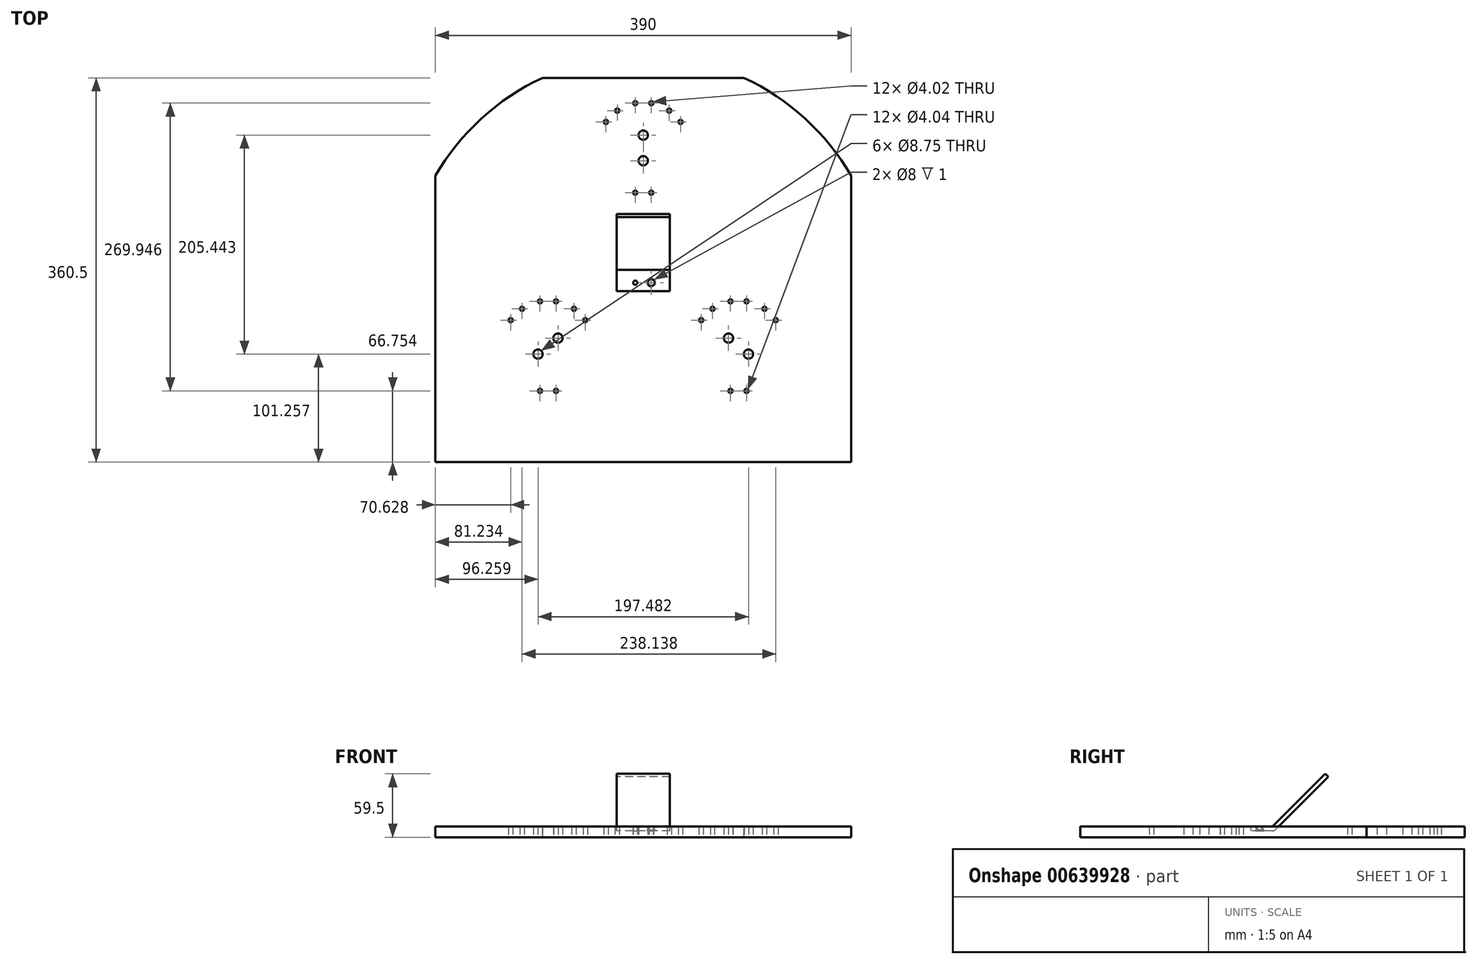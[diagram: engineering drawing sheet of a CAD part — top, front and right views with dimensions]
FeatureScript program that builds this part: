
annotation { "Feature Type Name" : "Feature", "Feature Type Description" : "" }
export const myFeature = defineFeature(function(context is Context, id is Id, definition is map)
    precondition{}
    {
        {
            var Q0;
            Q0=qCreatedBy(makeId("Top.planeOp"),FACE);
            var sketch = newSketch(context, id + "F0", { "sketchPlane" : qUnion([Q0])});
            skLineSegment(sketch, "E0.bottom", {"start": v(195, -180.25) * mm, "end": v(-195, -180.25) * mm});
            skLineSegment(sketch, "E0.left", {"start": v(195, -180.25) * mm, "end": v(195, 88.25) * mm});
            skLineSegment(sketch, "E0.right", {"start": v(-195, -180.25) * mm, "end": v(-195, 88.25) * mm});
            skLineSegment(sketch, "E1", {"start": v(-94.38, 180.25) * mm, "end": v(94.38, 180.25) * mm});
            skArc(sketch, "E2", {"start": v(-94.38, 180.25) * mm, "mid": v(-151.82, 142.06) * mm, "end": v(-195, 88.25) * mm});
            skArc(sketch, "E3", {"start": v(195, 88.25) * mm, "mid": v(151.82, 142.06) * mm, "end": v(94.38, 180.25) * mm});
            skCircle(sketch, "E4", {"center": v(0, 0) * mm, "radius": 126.45 * mm, "construction": true});
            skCircle(sketch, "E5", {"center": v(0, 0) * mm, "radius": 102.45 * mm, "construction": true});
            skLineSegment(sketch, "E6", {"start": v(-98.74, -79) * mm, "end": v(0, 0) * mm, "construction": true});
            skLineSegment(sketch, "E7", {"start": v(98.74, -79) * mm, "end": v(0, 0) * mm, "construction": true});
            skPoint(sketch, "E8", {"position": v(0, 126.45) * mm});
            skPoint(sketch, "E9", {"position": v(0, 102.45) * mm});
            skPoint(sketch, "E10", {"position": v(80, -64) * mm});
            skPoint(sketch, "E11", {"position": v(98.74, -79) * mm});
            skPoint(sketch, "E12", {"position": v(-80, -64) * mm});
            skPoint(sketch, "E13", {"position": v(-98.74, -79) * mm});
            skSolve(sketch);
        }
        {
            var Q0;
            Q0 = qSketchRegion(id + "F0", true);
            extrude(context, id + "F1", {"entities" : qUnion([Q0]), "oppositeDirection" : true, "depth" : 10 * mm, "offsetDistance" : 25 * mm});
        }
        {
            var Q0;
            Q0=sQuery(id+"F0.wireOp",VERTEX,"E8");
            var Q1;
            Q1=sQuery(id+"F0.wireOp",VERTEX,"E9");
            var Q2;
            Q2=sQuery(id+"F0.wireOp",VERTEX,"E12");
            var Q3;
            Q3=sQuery(id+"F0.wireOp",VERTEX,"E13");
            var Q4;
            Q4=sQuery(id+"F0.wireOp",VERTEX,"E10");
            var Q5;
            Q5=sQuery(id+"F0.wireOp",VERTEX,"E11");
            var Q6;
            Q6=makeQuery(id+"F1.opExtrude","SWEPT_BODY",BODY,{"disambiguationData":[OSD([sQuery(id+"F0.wireOp",EDGE,"E0.bottom"),sQuery(id+"F0.wireOp",EDGE,"E0.left"),sQuery(id+"F0.wireOp",EDGE,"E0.right"),sQuery(id+"F0.wireOp",EDGE,"E1"),sQuery(id+"F0.wireOp",EDGE,"E2"),sQuery(id+"F0.wireOp",EDGE,"E3")])]});
            hole(context, id + "F2", {"style" : HoleStyle.SIMPLE, "endStyle" : HoleEndStyle.THROUGH, "holeDiameter" : 8.75 * mm, "majorDiameter" : 5 * mm, "isTappedThrough" : true, "tappedDepth" : 12 * mm, "tapClearance" : 3, "locations" : qUnion([Q0, Q1, Q2, Q3, Q4, Q5]), "scope" : qUnion([Q6]), "startStyle" : HoleStartStyle.PART});
        }
        {
            var Q0;
            Q0=makeQuery(id+"F1.opExtrude","CAP_FACE",FACE,{"disambiguationData":[OSD([sQuery(id+"F0.wireOp",EDGE,"E0.bottom"),sQuery(id+"F0.wireOp",EDGE,"E0.left"),sQuery(id+"F0.wireOp",EDGE,"E0.right"),sQuery(id+"F0.wireOp",EDGE,"xNgbPUBY-uuYC-CHOZ-C7bY-90BZvyAFI4Vc"),sQuery(id+"F0.wireOp",EDGE,"pYRuWuoG-lrcK-cojv-Qarx-NnTwJ9ShBMCn"),sQuery(id+"F0.wireOp",EDGE,"e0wAC1A8-toIX-Gtfu-GmEW-TRQK8LJyyQk8"),sQuery(id+"F0.wireOp",EDGE,"2FMPs9kU-bOJq-Ht3o-1aew-Xf9CLyV6Ygsu"),sQuery(id+"F0.wireOp",EDGE,"OQ8i2MKw-3ids-VtER-UMBf-tPz4OA3PYS6q"),sQuery(id+"F0.wireOp",EDGE,"hYeVSYyp-zt9g-Qamr-OxOk-HJPD7gPKY8dS"),sQuery(id+"F0.wireOp",EDGE,"E1"),sQuery(id+"F0.wireOp",EDGE,"E2"),sQuery(id+"F0.wireOp",EDGE,"E3")])],"isStart":true});
            var sketch = newSketch(context, id + "F3", { "sketchPlane" : qUnion([Q0])});
            skLineSegment(sketch, "E14", {"start": v(0, 126.45) * mm, "end": v(0, 102.45) * mm, "construction": true});
            skPoint(sketch, "E15.1.0", {"position": v(7.5, 72.45) * mm});
            skLineSegment(sketch, "E15.1.1", {"start": v(7.5, 72.45) * mm, "end": v(-7.5, 72.45) * mm, "construction": true});
            skPoint(sketch, "E15.1.3", {"position": v(-7.5, 72.45) * mm});
            skPoint(sketch, "E16", {"position": v(0, 114.45) * mm});
            skPoint(sketch, "E17", {"position": v(0, 72.45) * mm});
            skPoint(sketch, "E18.1.0", {"position": v(-35, 138.85) * mm});
            skLineSegment(sketch, "E18.1.1", {"start": v(-35, 138.85) * mm, "end": v(-24.4, 149.45) * mm, "construction": true});
            skPoint(sketch, "E18.1.2", {"position": v(-24.4, 149.45) * mm});
            skPoint(sketch, "E18.1.3", {"position": v(-29.7, 144.15) * mm});
            skLineSegment(sketch, "E18.anchor1", {"start": v(0, 114.45) * mm, "end": v(0, 72.45) * mm, "construction": true});
            skLineSegment(sketch, "E18.anchor2", {"start": v(0, 114.45) * mm, "end": v(-29.7, 144.15) * mm, "construction": true});
            skPoint(sketch, "E19.1.0", {"position": v(7.5, 156.45) * mm});
            skLineSegment(sketch, "E19.1.1", {"start": v(-7.5, 156.45) * mm, "end": v(7.5, 156.45) * mm, "construction": true});
            skPoint(sketch, "E19.1.2", {"position": v(0, 156.45) * mm});
            skPoint(sketch, "E19.1.3", {"position": v(-7.5, 156.45) * mm});
            skPoint(sketch, "E19.2.0", {"position": v(35, 138.85) * mm});
            skLineSegment(sketch, "E19.2.1", {"start": v(24.4, 149.45) * mm, "end": v(35, 138.85) * mm, "construction": true});
            skPoint(sketch, "E19.2.2", {"position": v(29.7, 144.15) * mm});
            skPoint(sketch, "E19.2.3", {"position": v(24.4, 149.45) * mm});
            skLineSegment(sketch, "E19.anchor2", {"start": v(0, 114.45) * mm, "end": v(29.7, 144.15) * mm, "construction": true});
            skPoint(sketch, "E20.1.0", {"position": v(96.87, -113.5) * mm});
            skLineSegment(sketch, "E20.1.1", {"start": v(96.87, -113.5) * mm, "end": v(81.87, -113.5) * mm, "construction": true});
            skPoint(sketch, "E20.1.3", {"position": v(81.87, -113.5) * mm});
            skPoint(sketch, "E21", {"position": v(89.37, -71.5) * mm});
            skPoint(sketch, "E22", {"position": v(89.37, -113.5) * mm});
            skPoint(sketch, "E23.1.0", {"position": v(54.37, -47.1) * mm});
            skLineSegment(sketch, "E23.1.1", {"start": v(54.37, -47.1) * mm, "end": v(64.98, -36.5) * mm, "construction": true});
            skPoint(sketch, "E23.1.2", {"position": v(64.98, -36.5) * mm});
            skPoint(sketch, "E23.1.3", {"position": v(59.67, -41.8) * mm});
            skLineSegment(sketch, "E23.anchor1", {"start": v(89.37, -71.5) * mm, "end": v(89.37, -113.5) * mm, "construction": true});
            skLineSegment(sketch, "E23.anchor2", {"start": v(89.37, -71.5) * mm, "end": v(59.67, -41.8) * mm, "construction": true});
            skPoint(sketch, "E24.1.0", {"position": v(96.87, -29.5) * mm});
            skLineSegment(sketch, "E24.1.1", {"start": v(81.87, -29.5) * mm, "end": v(96.87, -29.5) * mm, "construction": true});
            skPoint(sketch, "E24.1.2", {"position": v(89.37, -29.5) * mm});
            skPoint(sketch, "E24.1.3", {"position": v(81.87, -29.5) * mm});
            skPoint(sketch, "E24.2.0", {"position": v(124.37, -47.1) * mm});
            skLineSegment(sketch, "E24.2.1", {"start": v(113.77, -36.5) * mm, "end": v(124.37, -47.1) * mm, "construction": true});
            skPoint(sketch, "E24.2.2", {"position": v(119.07, -41.8) * mm});
            skPoint(sketch, "E24.2.3", {"position": v(113.77, -36.5) * mm});
            skLineSegment(sketch, "E24.anchor2", {"start": v(89.37, -71.5) * mm, "end": v(119.07, -41.8) * mm, "construction": true});
            skLineSegment(sketch, "E25", {"start": v(80, -64) * mm, "end": v(98.74, -79) * mm, "construction": true});
            skPoint(sketch, "E26.1.0", {"position": v(-81.87, -113.5) * mm});
            skLineSegment(sketch, "E26.1.1", {"start": v(-81.87, -113.5) * mm, "end": v(-96.87, -113.5) * mm, "construction": true});
            skPoint(sketch, "E26.1.3", {"position": v(-96.87, -113.5) * mm});
            skPoint(sketch, "E27", {"position": v(-89.37, -71.5) * mm});
            skPoint(sketch, "E28", {"position": v(-89.37, -113.5) * mm});
            skPoint(sketch, "E29.1.0", {"position": v(-124.37, -47.1) * mm});
            skLineSegment(sketch, "E29.1.1", {"start": v(-124.37, -47.1) * mm, "end": v(-113.77, -36.5) * mm, "construction": true});
            skPoint(sketch, "E29.1.2", {"position": v(-113.77, -36.5) * mm});
            skPoint(sketch, "E29.1.3", {"position": v(-119.07, -41.8) * mm});
            skLineSegment(sketch, "E29.anchor1", {"start": v(-89.37, -71.5) * mm, "end": v(-89.37, -113.5) * mm, "construction": true});
            skLineSegment(sketch, "E29.anchor2", {"start": v(-89.37, -71.5) * mm, "end": v(-119.07, -41.8) * mm, "construction": true});
            skPoint(sketch, "E30.1.0", {"position": v(-81.87, -29.5) * mm});
            skLineSegment(sketch, "E30.1.1", {"start": v(-96.87, -29.5) * mm, "end": v(-81.87, -29.5) * mm, "construction": true});
            skPoint(sketch, "E30.1.2", {"position": v(-89.37, -29.5) * mm});
            skPoint(sketch, "E30.1.3", {"position": v(-96.87, -29.5) * mm});
            skPoint(sketch, "E30.2.0", {"position": v(-54.37, -47.1) * mm});
            skLineSegment(sketch, "E30.2.1", {"start": v(-64.98, -36.5) * mm, "end": v(-54.37, -47.1) * mm, "construction": true});
            skPoint(sketch, "E30.2.2", {"position": v(-59.67, -41.8) * mm});
            skPoint(sketch, "E30.2.3", {"position": v(-64.98, -36.5) * mm});
            skLineSegment(sketch, "E30.anchor2", {"start": v(-89.37, -71.5) * mm, "end": v(-59.67, -41.8) * mm, "construction": true});
            skLineSegment(sketch, "E31", {"start": v(-80, -64) * mm, "end": v(-98.74, -79) * mm, "construction": true});
            skSolve(sketch);
        }
        {
            var Q0;
            Q0=sQuery(id+"F3.wireOp",VERTEX,"E15.1.3");
            var Q1;
            Q1=sQuery(id+"F3.wireOp",VERTEX,"E20.1.3");
            var Q2;
            Q2=sQuery(id+"F3.wireOp",VERTEX,"E26.1.3");
            var Q3;
            Q3=sQuery(id+"F3.wireOp",VERTEX,"E29.1.2");
            var Q4;
            Q4=sQuery(id+"F3.wireOp",VERTEX,"E30.1.0");
            var Q5;
            Q5=sQuery(id+"F3.wireOp",VERTEX,"E30.2.0");
            var Q6;
            Q6=sQuery(id+"F3.wireOp",VERTEX,"E23.1.2");
            var Q7;
            Q7=sQuery(id+"F3.wireOp",VERTEX,"E24.1.0");
            var Q8;
            Q8=sQuery(id+"F3.wireOp",VERTEX,"E24.2.0");
            var Q9;
            Q9=sQuery(id+"F3.wireOp",VERTEX,"E18.1.2");
            var Q10;
            Q10=sQuery(id+"F3.wireOp",VERTEX,"E19.1.0");
            var Q11;
            Q11=sQuery(id+"F3.wireOp",VERTEX,"E19.2.0");
            var Q12;
            Q12=makeQuery(id+"F1.opExtrude","SWEPT_BODY",BODY,{"disambiguationData":[OSD([sQuery(id+"F0.wireOp",EDGE,"E0.bottom"),sQuery(id+"F0.wireOp",EDGE,"E0.left"),sQuery(id+"F0.wireOp",EDGE,"E0.right"),sQuery(id+"F0.wireOp",EDGE,"E1"),sQuery(id+"F0.wireOp",EDGE,"E2"),sQuery(id+"F0.wireOp",EDGE,"E3")])]});
            hole(context, id + "F4", {"style" : HoleStyle.SIMPLE, "endStyle" : HoleEndStyle.THROUGH, "holeDiameter" : 4 * mm, "majorDiameter" : 5 * mm, "isTappedThrough" : true, "tappedDepth" : 12 * mm, "tapClearance" : 3, "locations" : qUnion([Q0, Q1, Q2, Q3, Q4, Q5, Q6, Q7, Q8, Q9, Q10, Q11]), "scope" : qUnion([Q12]), "startStyle" : HoleStartStyle.PART});
        }
        {
            var Q0;
            Q0=sQuery(id+"F3.wireOp",VERTEX,"E15.1.0");
            var Q1;
            Q1=sQuery(id+"F3.wireOp",VERTEX,"E19.2.3");
            var Q2;
            Q2=sQuery(id+"F3.wireOp",VERTEX,"E19.1.3");
            var Q3;
            Q3=sQuery(id+"F3.wireOp",VERTEX,"E18.1.0");
            var Q4;
            Q4=sQuery(id+"F3.wireOp",VERTEX,"E26.1.0");
            var Q5;
            Q5=sQuery(id+"F3.wireOp",VERTEX,"E30.2.3");
            var Q6;
            Q6=sQuery(id+"F3.wireOp",VERTEX,"E30.1.3");
            var Q7;
            Q7=sQuery(id+"F3.wireOp",VERTEX,"E29.1.0");
            var Q8;
            Q8=sQuery(id+"F3.wireOp",VERTEX,"E20.1.0");
            var Q9;
            Q9=sQuery(id+"F3.wireOp",VERTEX,"E24.2.3");
            var Q10;
            Q10=sQuery(id+"F3.wireOp",VERTEX,"E24.1.3");
            var Q11;
            Q11=sQuery(id+"F3.wireOp",VERTEX,"E23.1.0");
            var Q12;
            Q12=makeQuery(id+"F1.opExtrude","SWEPT_BODY",BODY,{"disambiguationData":[OSD([sQuery(id+"F0.wireOp",EDGE,"E0.bottom"),sQuery(id+"F0.wireOp",EDGE,"E0.left"),sQuery(id+"F0.wireOp",EDGE,"E0.right"),sQuery(id+"F0.wireOp",EDGE,"E1"),sQuery(id+"F0.wireOp",EDGE,"E2"),sQuery(id+"F0.wireOp",EDGE,"E3")])]});
            hole(context, id + "F5", {"style" : HoleStyle.SIMPLE, "endStyle" : HoleEndStyle.THROUGH, "holeDiameter" : 4.04 * mm, "majorDiameter" : 5 * mm, "isTappedThrough" : true, "tappedDepth" : 12 * mm, "tapClearance" : 3, "locations" : qUnion([Q0, Q1, Q2, Q3, Q4, Q5, Q6, Q7, Q8, Q9, Q10, Q11]), "scope" : qUnion([Q12]), "startStyle" : HoleStartStyle.PART});
        }
        {
            var Q0;
            Q0=qCreatedBy(makeId("Right.planeOp"),FACE);
            var sketch = newSketch(context, id + "F6", { "sketchPlane" : qUnion([Q0])});
            skLineSegment(sketch, "E32", {"start": v(0, 0) * mm, "end": v(49.5, 49.5) * mm});
            skLineSegment(sketch, "E33", {"start": v(49.5, 49.5) * mm, "end": v(52.33, 46.67) * mm});
            skLineSegment(sketch, "E34", {"start": v(52.33, 46.67) * mm, "end": v(2.83, -2.83) * mm});
            skLineSegment(sketch, "E35", {"start": v(0, -4) * mm, "end": v(-20, -4) * mm});
            skLineSegment(sketch, "E36", {"start": v(-20, -4) * mm, "end": v(-20, 0) * mm});
            skLineSegment(sketch, "E37", {"start": v(-20, 0) * mm, "end": v(0, 0) * mm});
            skPoint(sketch, "E38.visualSharp", {"position": v(1.66, -4) * mm});
            skArc(sketch, "E38.filletArc", {"start": v(0, -4) * mm, "mid": v(1.53, -3.7) * mm, "end": v(2.83, -2.83) * mm});
            skSolve(sketch);
        }
        {
            var Q0;
            Q0 = qSketchRegion(id + "F6", true);
            extrude(context, id + "F7", {"entities" : qUnion([Q0]), "depth" : 50 * mm, "offsetDistance" : 25 * mm, "symmetric" : true});
        }
        {
            var Q0;
            Q0=makeQuery(id+"F7.opExtrude","SWEPT_FACE",FACE,{"disambiguationData":[OSD([sQuery(id+"F6.wireOp",EDGE,"E37")])]});
            var sketch = newSketch(context, id + "F8", { "sketchPlane" : qUnion([Q0])});
            skCircle(sketch, "E39", {"center": v(-7.5, -12) * mm, "radius": 2 * mm});
            skCircle(sketch, "E40", {"center": v(7.5, -12) * mm, "radius": 3.18 * mm});
            skSolve(sketch);
        }
        {
            var Q0;
            Q0 = qSketchRegion(id + "F8", true);
            extrude(context, id + "F9", {"entities" : qUnion([Q0]), "operationType" : NewBodyOperationType.REMOVE, "endBound" : BoundingType.UP_TO_NEXT, "oppositeDirection" : true, "depth" : 25 * mm, "offsetDistance" : 25 * mm});
        }
        {
            var Q0;
            Q0=makeQuery(id+"F7.opExtrude","SWEPT_FACE",FACE,{"disambiguationData":[OSD([sQuery(id+"F6.wireOp",EDGE,"E35")])]});
            var sketch = newSketch(context, id + "F10", { "sketchPlane" : qUnion([Q0])});
            skCircle(sketch, "E41", {"center": v(7.5, 12) * mm, "radius": 4 * mm});
            skSolve(sketch);
        }
        {
            var Q0;
            Q0 = qSketchRegion(id + "F10", true);
            extrude(context, id + "F11", {"entities" : qUnion([Q0]), "operationType" : NewBodyOperationType.REMOVE, "oppositeDirection" : true, "depth" : 1 * mm, "offsetDistance" : 25 * mm});
        }
    });
